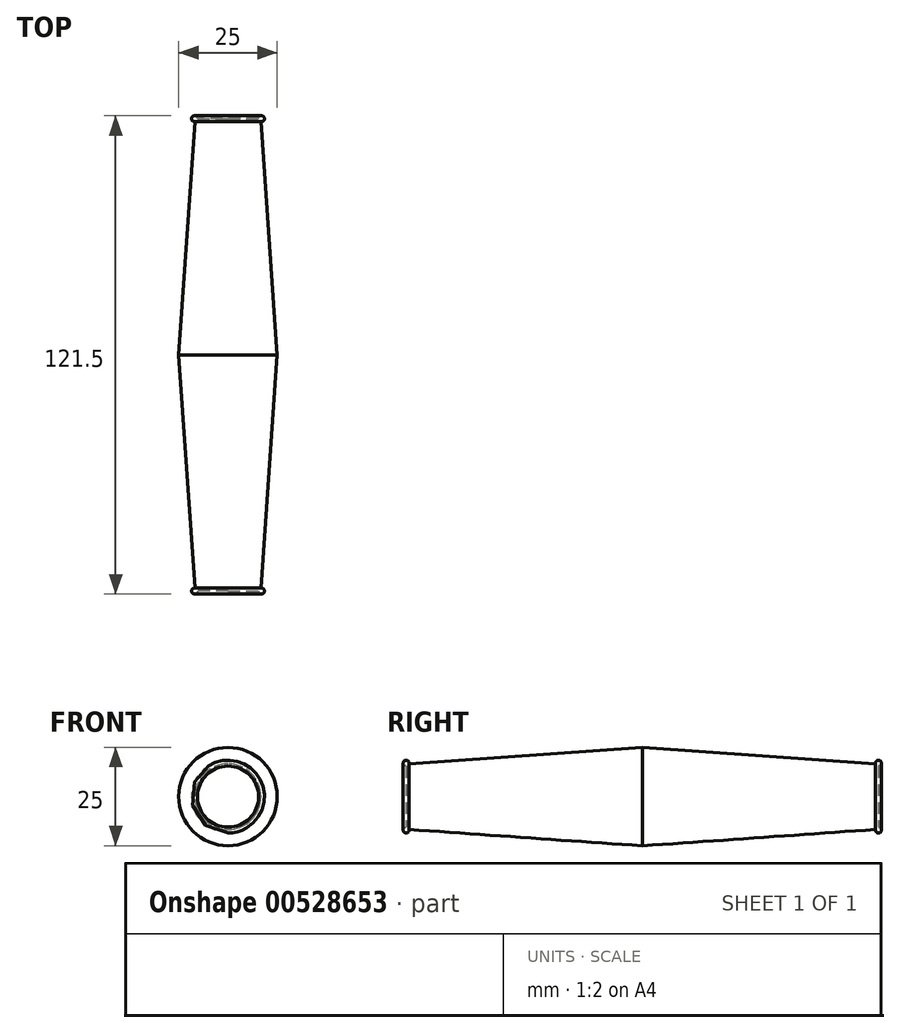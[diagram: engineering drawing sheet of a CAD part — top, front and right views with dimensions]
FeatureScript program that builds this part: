
annotation { "Feature Type Name" : "Feature", "Feature Type Description" : "" }
export const myFeature = defineFeature(function(context is Context, id is Id, definition is map)
    precondition{}
    {
        {
            var Q0;
            Q0=qCreatedBy(makeId("Front.planeOp"),FACE);
            var sketch = newSketch(context, id + "F0", { "sketchPlane" : qUnion([Q0])});
            skCircle(sketch, "E0", {"center": v(0, 0) * mm, "radius": 12.5 * mm});
            skSolve(sketch);
        }
        {
            var Q0;
            Q0 = qSketchRegion(id + "F0", true);
            extrude(context, id + "F1", {"entities" : qUnion([Q0]), "endBound" : BoundingType.SYMMETRIC, "depth" : 120 * mm, "offsetDistance" : 25 * mm, "hasDraft" : true, "draftAngle" : 4 * degree, "draftPullDirection" : true});
        }
        {
            var Q0;
            Q0=makeQuery(id+"F1.opExtrude","CAP_FACE",FACE,{"disambiguationData":[OSD([sQuery(id+"F0.wireOp",EDGE,"E0")])],"isStart":false});
            var sketch = newSketch(context, id + "F2", { "sketchPlane" : qUnion([Q0])});
            skCircle(sketch, "E1", {"center": v(0, 0) * mm, "radius": 8 * mm});
            skSolve(sketch);
        }
        {
            var Q0;
            Q0=qCreatedBy(makeId("Right.planeOp"),FACE);
            var sketch = newSketch(context, id + "F3", { "sketchPlane" : qUnion([Q0])});
            skCircle(sketch, "E2", {"center": v(-60, 8.5) * mm, "radius": 0.75 * mm});
            skSolve(sketch);
        }
        {
            var Q0;
            Q0 = qSketchRegion(id + "F3", true);
            var Q1;
            Q1 = qConstructionFilter(qBodyType(qCreatedBy(id + "F2" ,EDGE), BodyType.WIRE), ConstructionObject.NO);
            sweep(context, id + "F4", {"operationType" : NewBodyOperationType.ADD, "profiles" : qUnion([Q0]), "path" : qUnion([Q1])});
        }
        {
            var Q0;
            Q0=makeQuery(id+"F1.opExtrude","CAP_FACE",FACE,{"disambiguationData":[OSD([sQuery(id+"F0.wireOp",EDGE,"E0")])],"isStart":true});
            var sketch = newSketch(context, id + "F5", { "sketchPlane" : qUnion([Q0])});
            skCircle(sketch, "E3", {"center": v(0, 0) * mm, "radius": 8 * mm});
            skSolve(sketch);
        }
        {
            var Q0;
            Q0=qCreatedBy(makeId("Right.planeOp"),FACE);
            var sketch = newSketch(context, id + "F6", { "sketchPlane" : qUnion([Q0])});
            skCircle(sketch, "E4", {"center": v(60, 8.5) * mm, "radius": 0.75 * mm});
            skSolve(sketch);
        }
        {
            var Q0;
            Q0 = qSketchRegion(id + "F6", true);
            var Q1;
            Q1 = qConstructionFilter(qBodyType(qCreatedBy(id + "F5" ,EDGE), BodyType.WIRE), ConstructionObject.NO);
            sweep(context, id + "F7", {"operationType" : NewBodyOperationType.ADD, "profiles" : qUnion([Q0]), "path" : qUnion([Q1])});
        }
    });
